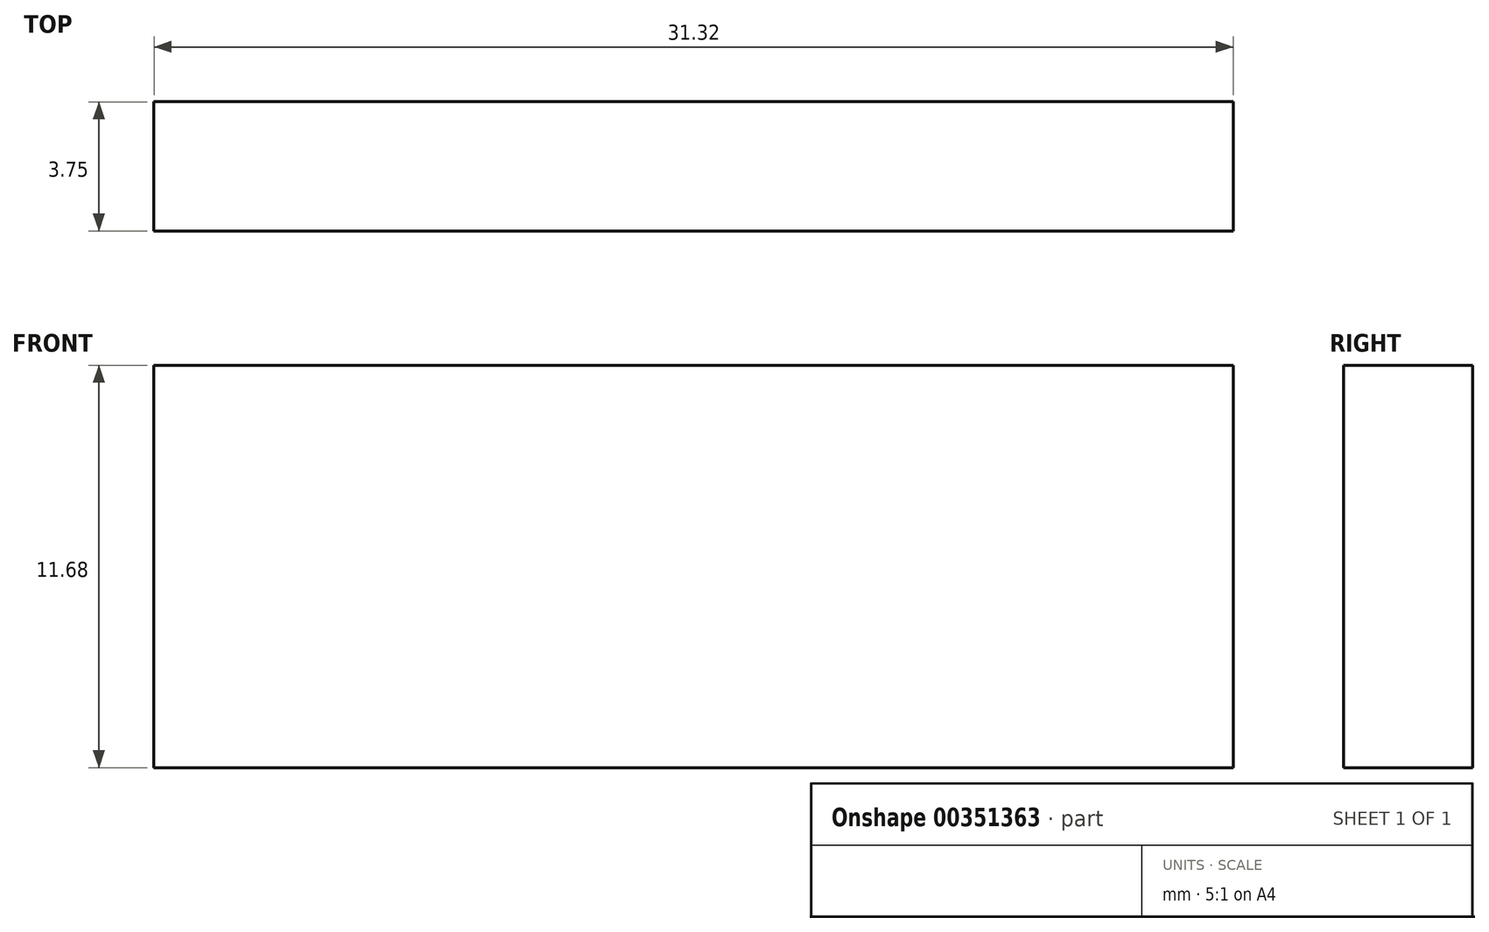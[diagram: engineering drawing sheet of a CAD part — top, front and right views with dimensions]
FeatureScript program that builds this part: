
annotation { "Feature Type Name" : "Feature", "Feature Type Description" : "" }
export const myFeature = defineFeature(function(context is Context, id is Id, definition is map)
    precondition{}
    {
        {
            var Q0;
            Q0=qCreatedBy(makeId("Front.planeOp"),FACE);
            var sketch = newSketch(context, id + "F0", { "sketchPlane" : qUnion([Q0])});
            skLineSegment(sketch, "E0", {"start": v(-15.66, -11.33) * mm, "end": v(15.66, -11.33) * mm});
            skLineSegment(sketch, "E1", {"start": v(15.66, -11.33) * mm, "end": v(15.66, 0) * mm});
            skLineSegment(sketch, "E2", {"start": v(-15.66, -11.33) * mm, "end": v(-15.66, 0) * mm});
            skArc(sketch, "E3", {"start": v(-15.66, 0) * mm, "mid": v(0, 15.66) * mm, "end": v(15.66, 0) * mm});
            skSolve(sketch);
        }
        {
            var Q0;
            Q0=qCreatedBy(makeId("Top.planeOp"),FACE);
            var sketch = newSketch(context, id + "F1", { "sketchPlane" : qUnion([Q0])});
            skLineSegment(sketch, "E4.bottom", {"start": v(-15.66, 0) * mm, "end": v(15.66, 0) * mm});
            skLineSegment(sketch, "E4.top", {"start": v(-15.66, 3.75) * mm, "end": v(15.66, 3.75) * mm});
            skLineSegment(sketch, "E4.left", {"start": v(-15.66, 0) * mm, "end": v(-15.66, 3.75) * mm});
            skLineSegment(sketch, "E4.right", {"start": v(15.66, 0) * mm, "end": v(15.66, 3.75) * mm});
            skSolve(sketch);
        }
        {
            var Q0;
            Q0 = qSketchRegion(id + "F1", true);
            extrude(context, id + "F2", {"entities" : qUnion([Q0]), "oppositeDirection" : true, "depth" : 11.68 * mm});
        }
    });
